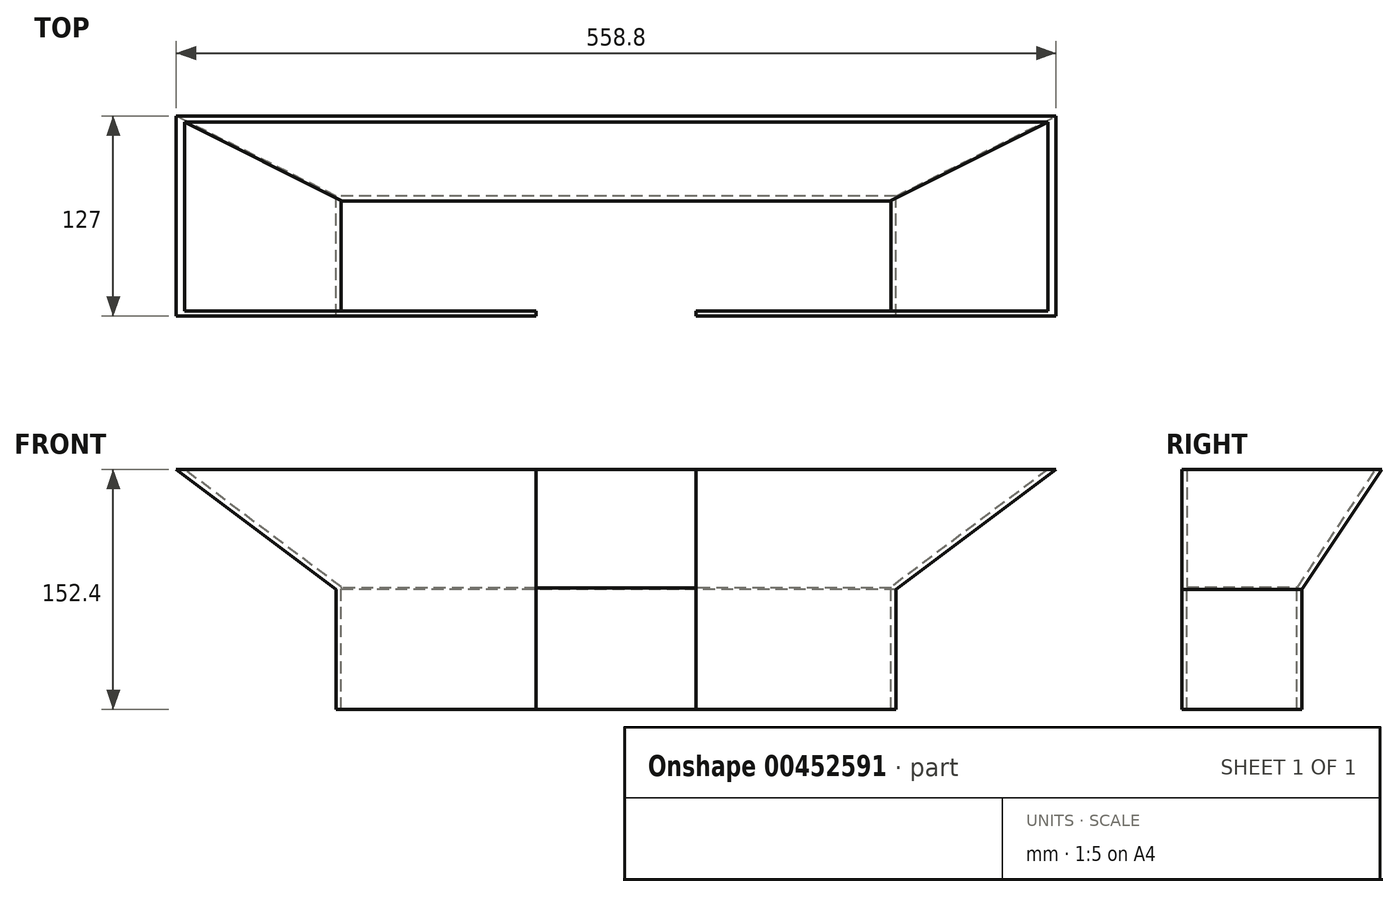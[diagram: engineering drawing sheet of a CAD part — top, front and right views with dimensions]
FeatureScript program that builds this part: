
annotation { "Feature Type Name" : "Feature", "Feature Type Description" : "" }
export const myFeature = defineFeature(function(context is Context, id is Id, definition is map)
    precondition{}
    {
        {
            var Q0;
            Q0=qCreatedBy(makeId("Right.planeOp"),FACE);
            var sketch = newSketch(context, id + "F0", { "sketchPlane" : qUnion([Q0])});
            skLineSegment(sketch, "E0.bottom", {"start": v(0, 0) * mm, "end": v(76.2, 0) * mm});
            skLineSegment(sketch, "E0.top", {"start": v(0, 152.4) * mm, "end": v(76.2, 152.4) * mm});
            skLineSegment(sketch, "E0.left", {"start": v(0, 0) * mm, "end": v(0, 152.4) * mm});
            skLineSegment(sketch, "E0.right", {"start": v(76.2, 0) * mm, "end": v(76.2, 152.4) * mm});
            skLineSegment(sketch, "E1", {"start": v(76.2, 152.4) * mm, "end": v(127, 152.4) * mm});
            skLineSegment(sketch, "E2", {"start": v(127, 152.4) * mm, "end": v(76.2, 76.2) * mm});
            skSolve(sketch);
        }
        {
            var Q0;
            Q0=qSketchRegion(id+"F0",true);
            extrude(context, id + "F1", {"entities" : qUnion([Q0]), "depth" : 355.6 * mm});
        }
        {
            var Q0;
            Q0=makeQuery(id+"F1.opExtrude","SWEPT_FACE",FACE,{"disambiguationData":[OSD([sQuery(id+"F0.wireOp",EDGE,"E0.left")])]});
            var sketch = newSketch(context, id + "F2", { "sketchPlane" : qUnion([Q0])});
            skLineSegment(sketch, "E3.bottom", {"start": v(355.6, 152.4) * mm, "end": v(457.2, 152.4) * mm});
            skLineSegment(sketch, "E3.top", {"start": v(355.6, 76.2) * mm, "end": v(457.2, 76.2) * mm});
            skLineSegment(sketch, "E3.left", {"start": v(355.6, 152.4) * mm, "end": v(355.6, 76.2) * mm});
            skLineSegment(sketch, "E3.right", {"start": v(457.2, 152.4) * mm, "end": v(457.2, 76.2) * mm});
            skLineSegment(sketch, "E4", {"start": v(457.2, 152.4) * mm, "end": v(355.6, 76.2) * mm});
            skLineSegment(sketch, "E5.bottom", {"start": v(0, 152.4) * mm, "end": v(-101.6, 152.4) * mm});
            skLineSegment(sketch, "E5.top", {"start": v(0, 76.2) * mm, "end": v(-101.6, 76.2) * mm});
            skLineSegment(sketch, "E5.left", {"start": v(0, 152.4) * mm, "end": v(0, 76.2) * mm});
            skLineSegment(sketch, "E5.right", {"start": v(-101.6, 152.4) * mm, "end": v(-101.6, 76.2) * mm});
            skLineSegment(sketch, "E6", {"start": v(0, 76.2) * mm, "end": v(-101.6, 152.4) * mm});
            skLineSegment(sketch, "E7.bottom", {"start": v(0, 152.4) * mm, "end": v(355.6, 152.4) * mm});
            skLineSegment(sketch, "E7.top", {"start": v(0, 76.2) * mm, "end": v(355.6, 76.2) * mm});
            skSolve(sketch);
        }
        {
            var Q0;
            Q0=makeQuery(id+"F2.imprint","IMPRINT",FACE,{"disambiguationData":[TD([[makeQuery(id+"F2.imprint","IMPRINT",EDGE,{"derivedFrom":sQuery(id+"F2.wireOp",EDGE,"E3.bottom")}),-1.0]])]});
            var Q1;
            Q1=makeQuery(id+"F2.imprint","IMPRINT",FACE,{"disambiguationData":[TD([[makeQuery(id+"F2.imprint","IMPRINT",EDGE,{"derivedFrom":sQuery(id+"F2.wireOp",EDGE,"E5.bottom")}),1.0]])]});
            var Q2;
            Q2=makeQuery(id+"F2.imprint","IMPRINT",FACE,{"disambiguationData":[TD([[makeQuery(id+"F2.imprint","IMPRINT",EDGE,{"derivedFrom":sQuery(id+"F2.wireOp",EDGE,"E7.bottom")}),1.0]])]});
            extrude(context, id + "F3", {"entities" : qUnion([Q0, Q1, Q2]), "operationType" : NewBodyOperationType.ADD, "oppositeDirection" : true, "depth" : 127 * mm});
        }
        {
            var Q0;
            Q0=makeQuery(id+"F1.opExtrude","CAP_FACE",FACE,{"disambiguationData":[OSD([sQuery(id+"F0.wireOp",EDGE,"E0.bottom"),sQuery(id+"F0.wireOp",EDGE,"E0.top"),sQuery(id+"F0.wireOp",EDGE,"E0.left"),sQuery(id+"F0.wireOp",EDGE,"E0.right"),sQuery(id+"F0.wireOp",EDGE,"E1"),sQuery(id+"F0.wireOp",EDGE,"E2")])],"isStart":false});
            var sketch = newSketch(context, id + "F4", { "sketchPlane" : qUnion([Q0])});
            skLineSegment(sketch, "E8", {"start": v(127, 76.2) * mm, "end": v(127, 152.4) * mm});
            skLineSegment(sketch, "E9", {"start": v(127, 76.2) * mm, "end": v(76.2, 76.2) * mm});
            skLineSegment(sketch, "E10", {"start": v(76.2, 76.2) * mm, "end": v(127, 152.4) * mm});
            skSolve(sketch);
        }
        {
            var Q0;
            Q0=qSketchRegion(id+"F4",true);
            extrude(context, id + "F5", {"entities" : qUnion([Q0]), "operationType" : NewBodyOperationType.REMOVE, "endBound" : BoundingType.THROUGH_ALL, "oppositeDirection" : true, "depth" : 25.4 * mm});
        }
        {
            var Q0;
            Q0=qSketchRegion(id+"F4",true);
            extrude(context, id + "F6", {"entities" : qUnion([Q0]), "operationType" : NewBodyOperationType.REMOVE, "endBound" : BoundingType.THROUGH_ALL, "depth" : 25.4 * mm});
        }
        {
            var Q0;
            Q0=makeQuery(id+"F3.boolean.opBoolean","MERGE",FACE,{"derivedFrom":[makeQuery(id+"F1.opExtrude","SWEPT_FACE",FACE,{"disambiguationData":[OSD([sQuery(id+"F0.wireOp",EDGE,"E0.top"),sQuery(id+"F0.wireOp",EDGE,"E1")])]}),makeQuery(id+"F3.opExtrude","SWEPT_FACE",FACE,{"disambiguationData":[OSD([sQuery(id+"F2.wireOp",EDGE,"E3.bottom"),sQuery(id+"F2.wireOp",EDGE,"E5.bottom"),sQuery(id+"F2.wireOp",EDGE,"E7.bottom")])]})]});
            var Q1;
            Q1=makeQuery(id+"F1.opExtrude","SWEPT_FACE",FACE,{"disambiguationData":[OSD([sQuery(id+"F0.wireOp",EDGE,"E0.bottom")])]});
            shell(context, id + "F7", {"entities" : qUnion([Q0, Q1]), "thickness" : 3.17 * mm});
        }
        {
            var Q0;
            Q0=makeQuery(id+"F1.opExtrude","SWEPT_FACE",FACE,{"disambiguationData":[OSD([sQuery(id+"F0.wireOp",EDGE,"E0.left")])]});
            var sketch = newSketch(context, id + "F8", { "sketchPlane" : qUnion([Q0])});
            skLineSegment(sketch, "E11.bottom", {"start": v(228.6, 152.4) * mm, "end": v(127, 152.4) * mm});
            skLineSegment(sketch, "E11.top", {"start": v(228.6, -76.2) * mm, "end": v(127, -76.2) * mm});
            skLineSegment(sketch, "E11.left", {"start": v(228.6, 152.4) * mm, "end": v(228.6, -76.2) * mm});
            skLineSegment(sketch, "E11.right", {"start": v(127, 152.4) * mm, "end": v(127, -76.2) * mm});
            skPoint(sketch, "E11.middle", {"position": v(177.8, 38.1) * mm});
            skPoint(sketch, "E11.middle.positionSnap0", {"position": v(355.6, 38.1) * mm});
            skPoint(sketch, "E11.middle.positionSnap1", {"position": v(177.8, 152.4) * mm});
            skPoint(sketch, "E11.centerSnap0", {"position": v(355.6, 38.1) * mm});
            skPoint(sketch, "E11.centerSnap1", {"position": v(177.8, 152.4) * mm});
            skSolve(sketch);
        }
        {
            var Q0;
            Q0=qSketchRegion(id+"F8",true);
            extrude(context, id + "F9", {"entities" : qUnion([Q0]), "operationType" : NewBodyOperationType.REMOVE, "oppositeDirection" : true, "depth" : 25.4 * mm});
        }
    });
